# Revit family: Cambio Wall Systems - Acoustic - Fabric 36x36
name_source: partatom
category: Generic Models
units: mm (PartAtom-declared; Revit-internal decimal feet)

## family parameters
Can host rebar = No
Cut with Voids When Loaded = No
Host = Face
Maintain Annotation Orientation = No
Part Type = Normal
Room Calculation Point = No
Round Connector Dimension = Use Diameter
Shared = No

## types (13) — shared parameters
Default Elevation = 4' - 0"

## per-type parameters (varying)
| type | Cambio Material |
| Fabric Color - ZINC | Cambio Fabric - Zinc |
| Fabric Color - TAUPE | Cambio Fabric - Taupe |
| Fabric Color - STERLING | Cambio Fabric - Sterling |
| Fabric Color - SLATE | Cambio Fabric - Sterling |
| Fabric Color - SHADOW | Cambio Fabric - Shadow |
| Fabric Color - SAND | Cambio Fabric - Sand |
| Fabric Color - PEBBLE | Cambio Fabric - Pebble |
| Fabric Color - PATINA | Cambio Fabric - Patina |
| Fabric Color - NECTAR | Cambio Fabric - Nectar |
| Fabric Color - FLINT | Cambio Fabric - Flint |
| Fabric Color - FELDSPAR | Cambio Fabric - Feldspar |
| Fabric Color - CHARCOAL | Cambio Fabric - Charcoal |
| Fabric Color - ALMOND | Cambio Fabric - Almond |

## geometry (parser evidence)
native form markers: Sweep x2
no freeform markers — native parametric forms only
